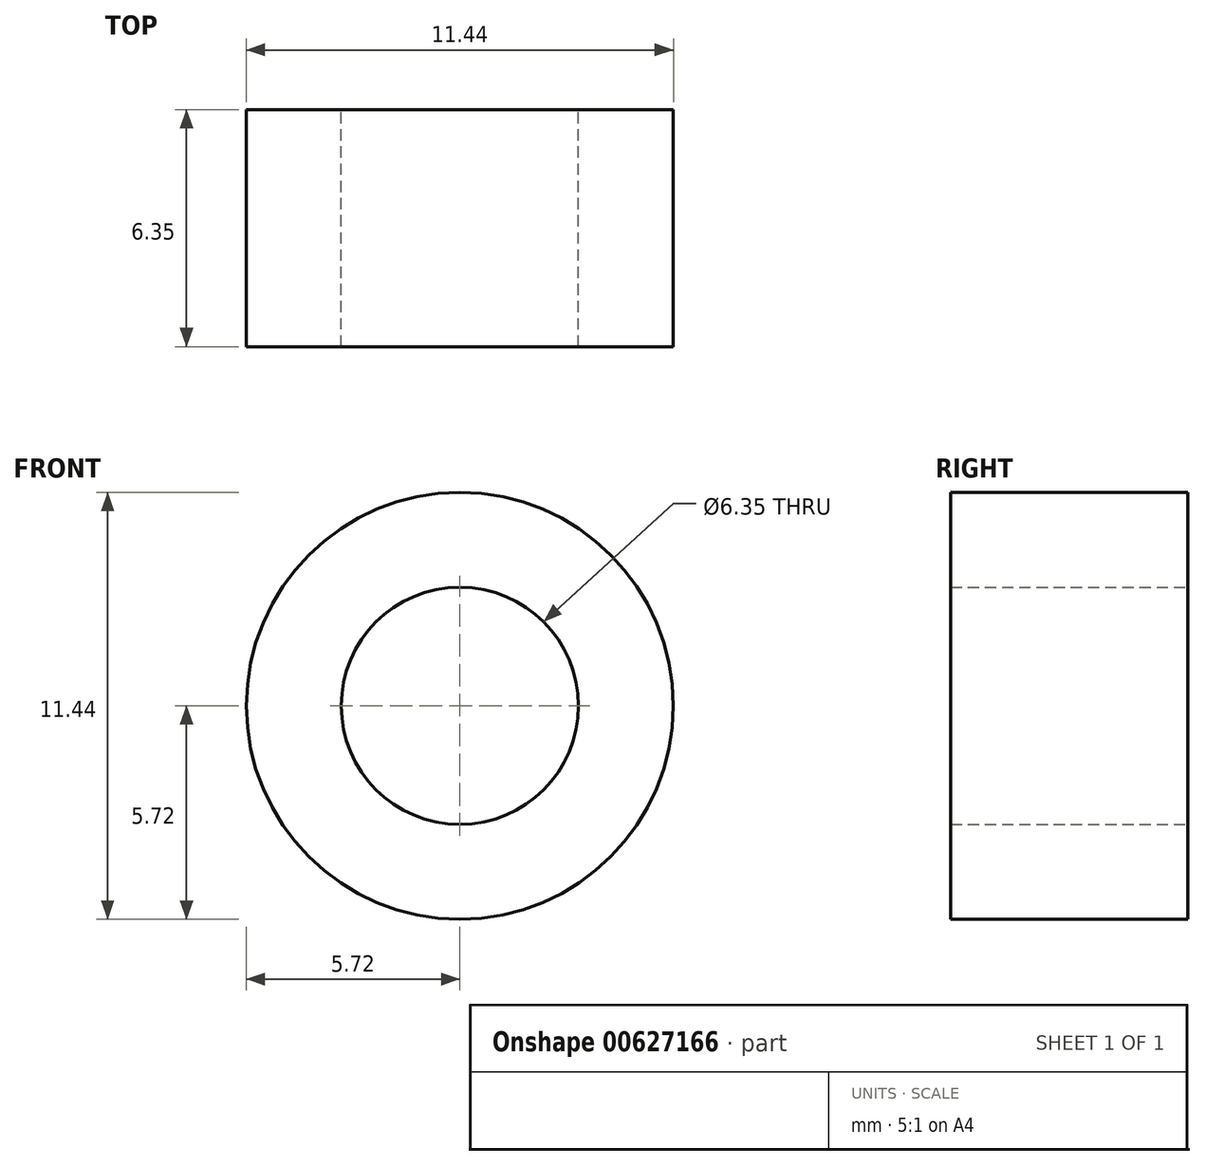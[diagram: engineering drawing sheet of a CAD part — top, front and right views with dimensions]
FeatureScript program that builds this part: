
annotation { "Feature Type Name" : "Feature", "Feature Type Description" : "" }
export const myFeature = defineFeature(function(context is Context, id is Id, definition is map)
    precondition{}
    {
        {
            var Q0;
            Q0=qCreatedBy(makeId("Front.planeOp"),FACE);
            var sketch = newSketch(context, id + "F0", { "sketchPlane" : qUnion([Q0])});
            skCircle(sketch, "E0", {"center": v(0, 0) * mm, "radius": 3.18 * mm});
            skCircle(sketch, "E1", {"center": v(0, 0) * mm, "radius": 5.72 * mm});
            skSolve(sketch);
        }
        {
            var Q0;
            Q0=makeQuery(id+"F0.imprint","IMPRINT",FACE,{"disambiguationData":[TD([[makeQuery(id+"F0.imprint","IMPRINT",EDGE,{"derivedFrom":sQuery(id+"F0.wireOp",EDGE,"E0")}),-1.0]])]});
            extrude(context, id + "F1", {"entities" : qUnion([Q0]), "depth" : 6.35 * mm, "offsetDistance" : 25.4 * mm});
        }
    });
